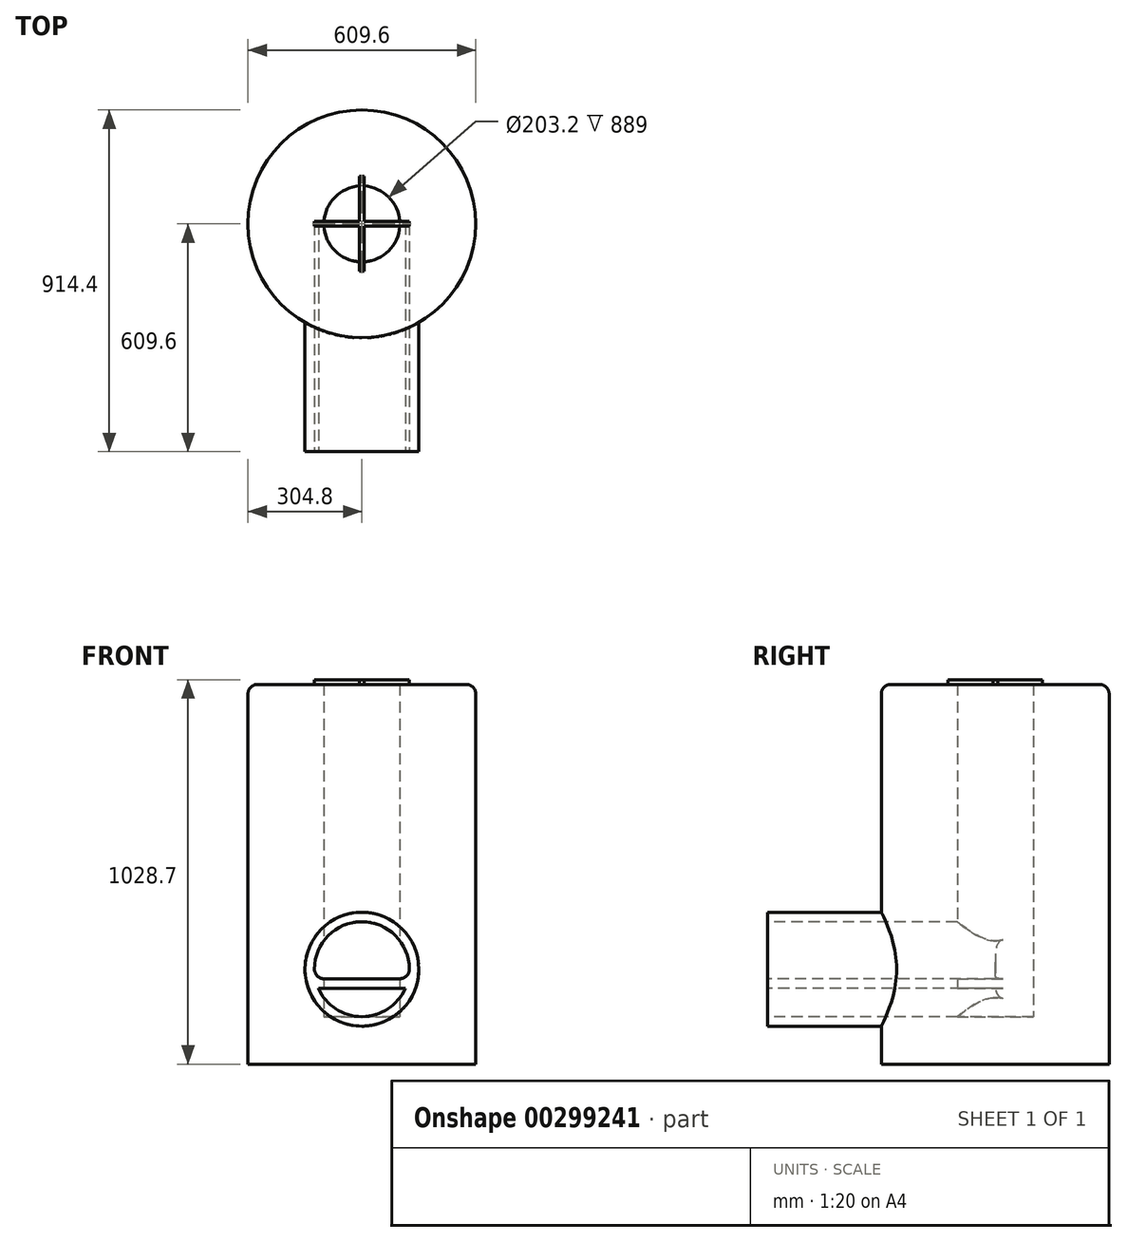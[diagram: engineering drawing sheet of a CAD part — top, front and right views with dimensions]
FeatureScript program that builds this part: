
annotation { "Feature Type Name" : "Feature", "Feature Type Description" : "" }
export const myFeature = defineFeature(function(context is Context, id is Id, definition is map)
    precondition{}
    {
        {
            var Q0;
            Q0=qCreatedBy(makeId("Front.planeOp"),FACE);
            var sketch = newSketch(context, id + "F0", { "sketchPlane" : qUnion([Q0])});
            skLineSegment(sketch, "E0", {"start": v(0, 101.6) * mm, "end": v(0, 889) * mm, "construction": true});
            skLineSegment(sketch, "E1", {"start": v(0, 889) * mm, "end": v(101.6, 889) * mm, "construction": true});
            skLineSegment(sketch, "E2", {"start": v(0, 0) * mm, "end": v(101.6, 0) * mm});
            skLineSegment(sketch, "E3", {"start": v(101.6, 889) * mm, "end": v(101.6, 0) * mm});
            skLineSegment(sketch, "E4", {"start": v(101.6, 889) * mm, "end": v(304.8, 889) * mm});
            skLineSegment(sketch, "E5", {"start": v(304.8, 889) * mm, "end": v(304.8, 0) * mm});
            skLineSegment(sketch, "E6", {"start": v(304.8, 0) * mm, "end": v(101.6, 0) * mm});
            skLineSegment(sketch, "E7", {"start": v(0, 0) * mm, "end": v(0, -127) * mm});
            skLineSegment(sketch, "E8", {"start": v(0, -127) * mm, "end": v(101.6, -127) * mm});
            skLineSegment(sketch, "E9", {"start": v(101.6, -127) * mm, "end": v(304.8, -127) * mm});
            skLineSegment(sketch, "E10", {"start": v(304.8, -127) * mm, "end": v(304.8, 0) * mm});
            skPoint(sketch, "E11.visualSharp", {"position": v(0, 0) * mm});
            skLineSegment(sketch, "E12", {"start": v(0, 101.6) * mm, "end": v(0, 0) * mm, "construction": true});
            skCircle(sketch, "E13", {"center": v(0, 101.6) * mm, "radius": 101.6 * mm, "construction": true});
            skSolve(sketch);
        }
        {
            var Q0;
            Q0=makeQuery(id+"F0.imprint","IMPRINT",FACE,{"disambiguationData":[TD([[makeQuery(id+"F0.imprint","IMPRINT",EDGE,{"derivedFrom":sQuery(id+"F0.wireOp",EDGE,"E3")}),1.0]])]});
            var Q1;
            Q1=makeQuery(id+"F0.imprint","IMPRINT",FACE,{"disambiguationData":[TD([[makeQuery(id+"F0.imprint","IMPRINT",EDGE,{"derivedFrom":sQuery(id+"F0.wireOp",EDGE,"E2")}),-1.0]])]});
            var Q2;
            {var subQ0=sQuery(id+"F0.wireOp",EDGE,"E2");Q2=makeQuery(id+"F0.imprint","IMPRINT",FACE,{"disambiguationData":[TD([[makeQuery(id+"F0.imprint","IMPRINT",EDGE,{"derivedFrom":subQ0}),1.0]])]});}
            var Q3;
            Q3=sQuery(id+"F0.wireOp",EDGE,"E0");
            revolve(context, id + "F1", {"entities" : qUnion([Q0, Q1, Q2]), "axis" : qUnion([Q3]), "revolveType" : RevolveType.FULL});
        }
        {
            var Q0;
            Q0=makeQuery(id+"F1.opRevolve","SWEPT_FACE",FACE,{"disambiguationData":[OSD([sQuery(id+"F0.wireOp",EDGE,"E4")])]});
            var sketch = newSketch(context, id + "F2", { "sketchPlane" : qUnion([Q0])});
            skLineSegment(sketch, "E14", {"start": v(0, 0) * mm, "end": v(0, -304.8) * mm, "construction": true});
            skLineSegment(sketch, "E15", {"start": v(304.8, 0) * mm, "end": v(304.8, -304.8) * mm, "construction": true});
            skLineSegment(sketch, "E16", {"start": v(-304.8, 0) * mm, "end": v(-304.8, -304.8) * mm, "construction": true});
            skLineSegment(sketch, "E17", {"start": v(-304.8, -304.8) * mm, "end": v(304.8, -304.8) * mm});
            skSolve(sketch);
        }
        {
            var Q0;
            Q0=sQuery(id+"F2.wireOp",EDGE,"E17");
            var Q1;
            Q1=makeQuery(id+"F1.opRevolve","SWEPT_FACE",FACE,{"disambiguationData":[OSD([sQuery(id+"F0.wireOp",EDGE,"E8"),sQuery(id+"F0.wireOp",EDGE,"E9")])]});
            extrude(context, id + "F3", {"bodyType" : ToolBodyType.SURFACE, "surfaceEntities" : qUnion([Q0]), "endBound" : BoundingType.UP_TO_SURFACE, "oppositeDirection" : true, "endBoundEntityFace" : qUnion([Q1]), "depth" : 289.56 * mm});
        }
        {
            var Q0;
            Q0=makeQuery(id+"F3.opExtrude","SWEPT_FACE",FACE,{"disambiguationData":[OSD([sQuery(id+"F2.wireOp",EDGE,"E17")])]});
            var sketch = newSketch(context, id + "F4", { "sketchPlane" : qUnion([Q0])});
            skLineSegment(sketch, "E18", {"start": v(0, 0) * mm, "end": v(0, 127) * mm, "construction": true});
            skCircle(sketch, "E19", {"center": v(0, 127) * mm, "radius": 152.4 * mm});
            skCircle(sketch, "E20", {"center": v(0, 127) * mm, "radius": 127 * mm});
            skLineSegment(sketch, "E21", {"start": v(124.43, 101.6) * mm, "end": v(-124.43, 101.6) * mm});
            skLineSegment(sketch, "E22", {"start": v(116.4, 76.2) * mm, "end": v(-116.4, 76.2) * mm});
            skSolve(sketch);
        }
        {
            var Q0;
            {var subQ0=sQuery(id+"F4.wireOp",EDGE,"E21");Q0=makeQuery(id+"F4.imprint","IMPRINT",FACE,{"disambiguationData":[TD([[makeQuery(id+"F4.imprint","IMPRINT",EDGE,{"derivedFrom":subQ0}),-1.0]])]});}
            var Q1;
            {var subQ0=sQuery(id+"F4.wireOp",EDGE,"E22");Q1=makeQuery(id+"F4.imprint","IMPRINT",FACE,{"disambiguationData":[TD([[makeQuery(id+"F4.imprint","IMPRINT",EDGE,{"derivedFrom":subQ0}),1.0]])]});}
            var Q2;
            Q2=makeQuery(id+"F1.opRevolve","SWEPT_FACE",FACE,{"disambiguationData":[OSD([sQuery(id+"F0.wireOp",EDGE,"E3")])]});
            var Q3;
            Q3=makeQuery(id+"F1.opRevolve","SWEPT_FACE",FACE,{"disambiguationData":[OSD([sQuery(id+"F0.wireOp",EDGE,"E5"),sQuery(id+"F0.wireOp",EDGE,"E10")])]});
            extrude(context, id + "F5", {"entities" : qUnion([Q0, Q1]), "operationType" : NewBodyOperationType.REMOVE, "endBoundEntityFace" : qUnion([Q2]), "depth" : 304.8 * mm});
        }
        {
            var Q0;
            Q0=makeQuery(id+"F4.imprint","IMPRINT",FACE,{"disambiguationData":[TD([[makeQuery(id+"F4.imprint","IMPRINT",EDGE,{"derivedFrom":sQuery(id+"F4.wireOp",EDGE,"E19")}),1.0]])]});
            var Q1;
            {var subQ0=sQuery(id+"F4.wireOp",EDGE,"E21");Q1=makeQuery(id+"F4.imprint","IMPRINT",FACE,{"disambiguationData":[TD([[makeQuery(id+"F4.imprint","IMPRINT",EDGE,{"derivedFrom":subQ0}),1.0]])]});}
            var Q2;
            Q2=makeQuery(id+"F1.opRevolve","SWEPT_FACE",FACE,{"disambiguationData":[OSD([sQuery(id+"F0.wireOp",EDGE,"E5"),sQuery(id+"F0.wireOp",EDGE,"E10")])]});
            extrude(context, id + "F6", {"entities" : qUnion([Q0, Q1]), "operationType" : NewBodyOperationType.ADD, "endBound" : BoundingType.UP_TO_SURFACE, "endBoundEntityFace" : qUnion([Q2]), "depth" : 25.4 * mm, "hasSecondDirection" : true, "secondDirectionOppositeDirection" : true, "secondDirectionDepth" : 304.8 * mm});
        }
        {
            var Q0;
            Q0=makeQuery(id+"F1.opRevolve","SWEPT_FACE",FACE,{"disambiguationData":[OSD([sQuery(id+"F0.wireOp",EDGE,"E4")])]});
            var sketch = newSketch(context, id + "F7", { "sketchPlane" : qUnion([Q0])});
            skSolve(sketch);
        }
        {
            var Q0;
            Q0=makeQuery(id+"F5.boolean.opBoolean","INTERSECT",EDGE,{"disambiguationData":[OD(0.0)],"derivedFrom":[makeQuery(id+"F1.opRevolve","SWEPT_FACE",FACE,{"disambiguationData":[OSD([sQuery(id+"F0.wireOp",EDGE,"E3")])]}),makeQuery(id+"F5.opExtrude","CAP_FACE",FACE,{"disambiguationData":[OSD([sQuery(id+"F4.wireOp",EDGE,"E20"),sQuery(id+"F4.wireOp",EDGE,"E21")])],"isStart":false})]});
            var Q1;
            Q1=makeQuery(id+"F5.boolean.opBoolean","INTERSECT",EDGE,{"disambiguationData":[OD(1.0)],"derivedFrom":[makeQuery(id+"F1.opRevolve","SWEPT_FACE",FACE,{"disambiguationData":[OSD([sQuery(id+"F0.wireOp",EDGE,"E3")])]}),makeQuery(id+"F5.opExtrude","CAP_FACE",FACE,{"disambiguationData":[OSD([sQuery(id+"F4.wireOp",EDGE,"E20"),sQuery(id+"F4.wireOp",EDGE,"E21")])],"isStart":false})]});
            var Q2;
            Q2=makeQuery(id+"F5.boolean.opBoolean","INTERSECT",EDGE,{"disambiguationData":[OD(1.0)],"derivedFrom":[makeQuery(id+"F1.opRevolve","SWEPT_FACE",FACE,{"disambiguationData":[OSD([sQuery(id+"F0.wireOp",EDGE,"E3")])]}),makeQuery(id+"F5.opExtrude","CAP_FACE",FACE,{"disambiguationData":[OSD([sQuery(id+"F4.wireOp",EDGE,"E20"),sQuery(id+"F4.wireOp",EDGE,"E22")])],"isStart":false})]});
            var Q3;
            Q3=makeQuery(id+"F5.boolean.opBoolean","INTERSECT",EDGE,{"disambiguationData":[OD(0.0)],"derivedFrom":[makeQuery(id+"F1.opRevolve","SWEPT_FACE",FACE,{"disambiguationData":[OSD([sQuery(id+"F0.wireOp",EDGE,"E3")])]}),makeQuery(id+"F5.opExtrude","CAP_FACE",FACE,{"disambiguationData":[OSD([sQuery(id+"F4.wireOp",EDGE,"E20"),sQuery(id+"F4.wireOp",EDGE,"E22")])],"isStart":false})]});
            fillet(context, id + "F8", {"entities" : qUnion([Q0, Q1, Q2, Q3]), "radius" : 25.4 * mm, "tangentPropagation" : true, "allowEdgeOverflow" : false});
        }
        {
            var Q0;
            Q0=makeQuery(id+"F1.opRevolve","SWEPT_EDGE",EDGE,{"disambiguationData":[OSD([sQuery(id+"F0.wireOp",EDGE,"E4"),sQuery(id+"F0.wireOp",EDGE,"E5")])]});
            var Q1;
            Q1=makeQuery(id+"F6.opExtrude","CAP_EDGE",EDGE,{"disambiguationData":[OSD([sQuery(id+"F4.wireOp",EDGE,"E19")])],"isStart":false});
            var Q2;
            {var subQ0=sQuery(id+"F4.wireOp",EDGE,"E21");var subQ1=sQuery(id+"F4.wireOp",EDGE,"E20");var subQ2=makeQuery(id+"F4.imprint","INTERSECT",VERTEX,{"disambiguationData":[OD(1.0)],"derivedFrom":[subQ1,subQ0]});Q2=makeQuery(id+"F6.boolean.opBoolean","MERGE",EDGE,{"derivedFrom":[makeQuery(id+"F5.boolean.opBoolean","COPY",EDGE,{"derivedFrom":makeQuery(id+"F5.opExtrude","SWEPT_EDGE",EDGE,{"disambiguationData":[OSD([subQ1,subQ0]),TDD([subQ2])]})}),makeQuery(id+"F6.opExtrude","SWEPT_EDGE",EDGE,{"disambiguationData":[OSD([subQ1,subQ0]),TDD([subQ2])]})]});}
            var Q3;
            {var subQ0=sQuery(id+"F4.wireOp",EDGE,"E21");var subQ1=sQuery(id+"F4.wireOp",EDGE,"E20");var subQ2=makeQuery(id+"F4.imprint","INTERSECT",VERTEX,{"disambiguationData":[OD(0.0)],"derivedFrom":[subQ1,subQ0]});Q3=makeQuery(id+"F6.boolean.opBoolean","MERGE",EDGE,{"derivedFrom":[makeQuery(id+"F5.boolean.opBoolean","COPY",EDGE,{"derivedFrom":makeQuery(id+"F5.opExtrude","SWEPT_EDGE",EDGE,{"disambiguationData":[OSD([subQ1,subQ0]),TDD([subQ2])]})}),makeQuery(id+"F6.opExtrude","SWEPT_EDGE",EDGE,{"disambiguationData":[OSD([subQ1,subQ0]),TDD([subQ2])]})]});}
            fillet(context, id + "F9", {"entities" : qUnion([Q0, Q1, Q2, Q3]), "radius" : 25.4 * mm, "tangentPropagation" : true, "allowEdgeOverflow" : false});
        }
        {
            var Q0;
            {var subQ0=sQuery(id+"F0.wireOp",EDGE,"E4");Q0=makeQuery(id+"F7.imprint","IMPRINT",FACE,{"disambiguationData":[TD([[makeQuery(id+"F7.imprint","IMPRINT",EDGE,{"derivedFrom":makeQuery(id+"F1.opRevolve","SWEPT_EDGE",EDGE,{"disambiguationData":[OSD([sQuery(id+"F0.wireOp",EDGE,"E3"),subQ0])]})}),1.0]])]});}
            var sketch = newSketch(context, id + "F10", { "sketchPlane" : qUnion([Q0])});
            skCircle(sketch, "E23", {"center": v(0, 0) * mm, "radius": 101.6 * mm, "construction": true});
            skCircle(sketch, "E24", {"center": v(0, 0) * mm, "radius": 6.35 * mm, "construction": true});
            skLineSegment(sketch, "E25", {"start": v(0, 6.35) * mm, "end": v(-126.84, 6.35) * mm});
            skLineSegment(sketch, "E26", {"start": v(0, 6.35) * mm, "end": v(126.84, 6.35) * mm});
            skLineSegment(sketch, "E27", {"start": v(6.35, 0) * mm, "end": v(6.35, 126.84) * mm});
            skLineSegment(sketch, "E28", {"start": v(6.35, 0) * mm, "end": v(6.35, -126.84) * mm});
            skLineSegment(sketch, "E29", {"start": v(-6.35, 0) * mm, "end": v(-6.35, 126.84) * mm});
            skLineSegment(sketch, "E30", {"start": v(-6.35, 0) * mm, "end": v(-6.35, -126.84) * mm});
            skLineSegment(sketch, "E31", {"start": v(0, -6.35) * mm, "end": v(126.84, -6.35) * mm});
            skLineSegment(sketch, "E32", {"start": v(0, -6.35) * mm, "end": v(-126.84, -6.35) * mm});
            skLineSegment(sketch, "E33", {"start": v(-126.84, 6.35) * mm, "end": v(-126.84, -6.35) * mm});
            skLineSegment(sketch, "E34", {"start": v(-6.35, 126.84) * mm, "end": v(6.35, 126.84) * mm});
            skLineSegment(sketch, "E35", {"start": v(126.84, 6.35) * mm, "end": v(126.84, -6.35) * mm});
            skLineSegment(sketch, "E36", {"start": v(-6.35, -126.84) * mm, "end": v(6.35, -126.84) * mm});
            skSolve(sketch);
        }
        {
            var Q0;
            {var subQ0=sQuery(id+"F10.wireOp",EDGE,"E34");Q0=makeQuery(id+"F10.imprint","IMPRINT",FACE,{"disambiguationData":[TD([[makeQuery(id+"F10.imprint","IMPRINT",EDGE,{"derivedFrom":subQ0}),-1.0]])]});}
            var Q1;
            {var subQ1=sQuery(id+"F10.wireOp",EDGE,"E26");var subQ6=sQuery(id+"F10.wireOp",EDGE,"E25");var subQ9=makeQuery(id+"F10.imprint","INTERSECT",VERTEX,{"derivedFrom":[subQ6,subQ1]});Q1=makeQuery(id+"F10.imprint","IMPRINT",FACE,{"disambiguationData":[TD([[makeQuery(id+"F10.imprint","IMPRINT",EDGE,{"disambiguationData":[TD([[subQ9,-1.0]])],"derivedFrom":subQ6}),-1.0]])]});}
            var Q2;
            {var subQ0=sQuery(id+"F10.wireOp",EDGE,"E28");var subQ1=sQuery(id+"F10.wireOp",EDGE,"E27");var subQ2=makeQuery(id+"F10.imprint","INTERSECT",VERTEX,{"derivedFrom":[subQ1,subQ0]});Q2=makeQuery(id+"F10.imprint","IMPRINT",FACE,{"disambiguationData":[TD([[makeQuery(id+"F10.imprint","IMPRINT",EDGE,{"disambiguationData":[TD([[subQ2,-1.0]])],"derivedFrom":subQ1}),-1.0]])]});}
            var Q3;
            {var subQ5=sQuery(id+"F10.wireOp",EDGE,"E26");var subQ7=sQuery(id+"F10.wireOp",EDGE,"E25");var subQ8=makeQuery(id+"F10.imprint","INTERSECT",VERTEX,{"derivedFrom":[subQ7,subQ5]});Q3=makeQuery(id+"F10.imprint","IMPRINT",FACE,{"disambiguationData":[TD([[makeQuery(id+"F10.imprint","IMPRINT",EDGE,{"disambiguationData":[TD([[subQ8,-1.0]])],"derivedFrom":subQ7}),1.0]])]});}
            var Q4;
            {var subQ0=sQuery(id+"F10.wireOp",EDGE,"E30");var subQ1=sQuery(id+"F10.wireOp",EDGE,"E29");var subQ2=makeQuery(id+"F10.imprint","INTERSECT",VERTEX,{"derivedFrom":[subQ1,subQ0]});Q4=makeQuery(id+"F10.imprint","IMPRINT",FACE,{"disambiguationData":[TD([[makeQuery(id+"F10.imprint","IMPRINT",EDGE,{"disambiguationData":[TD([[subQ2,-1.0]])],"derivedFrom":subQ1}),1.0]])]});}
            var Q5;
            {var subQ0=sQuery(id+"F10.wireOp",EDGE,"E35");Q5=makeQuery(id+"F10.imprint","IMPRINT",FACE,{"disambiguationData":[TD([[makeQuery(id+"F10.imprint","IMPRINT",EDGE,{"derivedFrom":subQ0}),-1.0]])]});}
            var Q6;
            {var subQ0=sQuery(id+"F10.wireOp",EDGE,"E33");Q6=makeQuery(id+"F10.imprint","IMPRINT",FACE,{"disambiguationData":[TD([[makeQuery(id+"F10.imprint","IMPRINT",EDGE,{"derivedFrom":subQ0}),1.0]])]});}
            var Q7;
            {var subQ0=sQuery(id+"F10.wireOp",EDGE,"E32");var subQ1=sQuery(id+"F10.wireOp",EDGE,"E31");var subQ2=makeQuery(id+"F10.imprint","INTERSECT",VERTEX,{"derivedFrom":[subQ1,subQ0]});Q7=makeQuery(id+"F10.imprint","IMPRINT",FACE,{"disambiguationData":[TD([[makeQuery(id+"F10.imprint","IMPRINT",EDGE,{"disambiguationData":[TD([[subQ2,-1.0]])],"derivedFrom":subQ1}),-1.0]])]});}
            var Q8;
            {var subQ0=sQuery(id+"F10.wireOp",EDGE,"E36");Q8=makeQuery(id+"F10.imprint","IMPRINT",FACE,{"disambiguationData":[TD([[makeQuery(id+"F10.imprint","IMPRINT",EDGE,{"derivedFrom":subQ0}),1.0]])]});}
            extrude(context, id + "F11", {"entities" : qUnion([Q0, Q1, Q2, Q3, Q4, Q5, Q6, Q7, Q8]), "operationType" : NewBodyOperationType.ADD, "depth" : 12.7 * mm});
        }
    });
